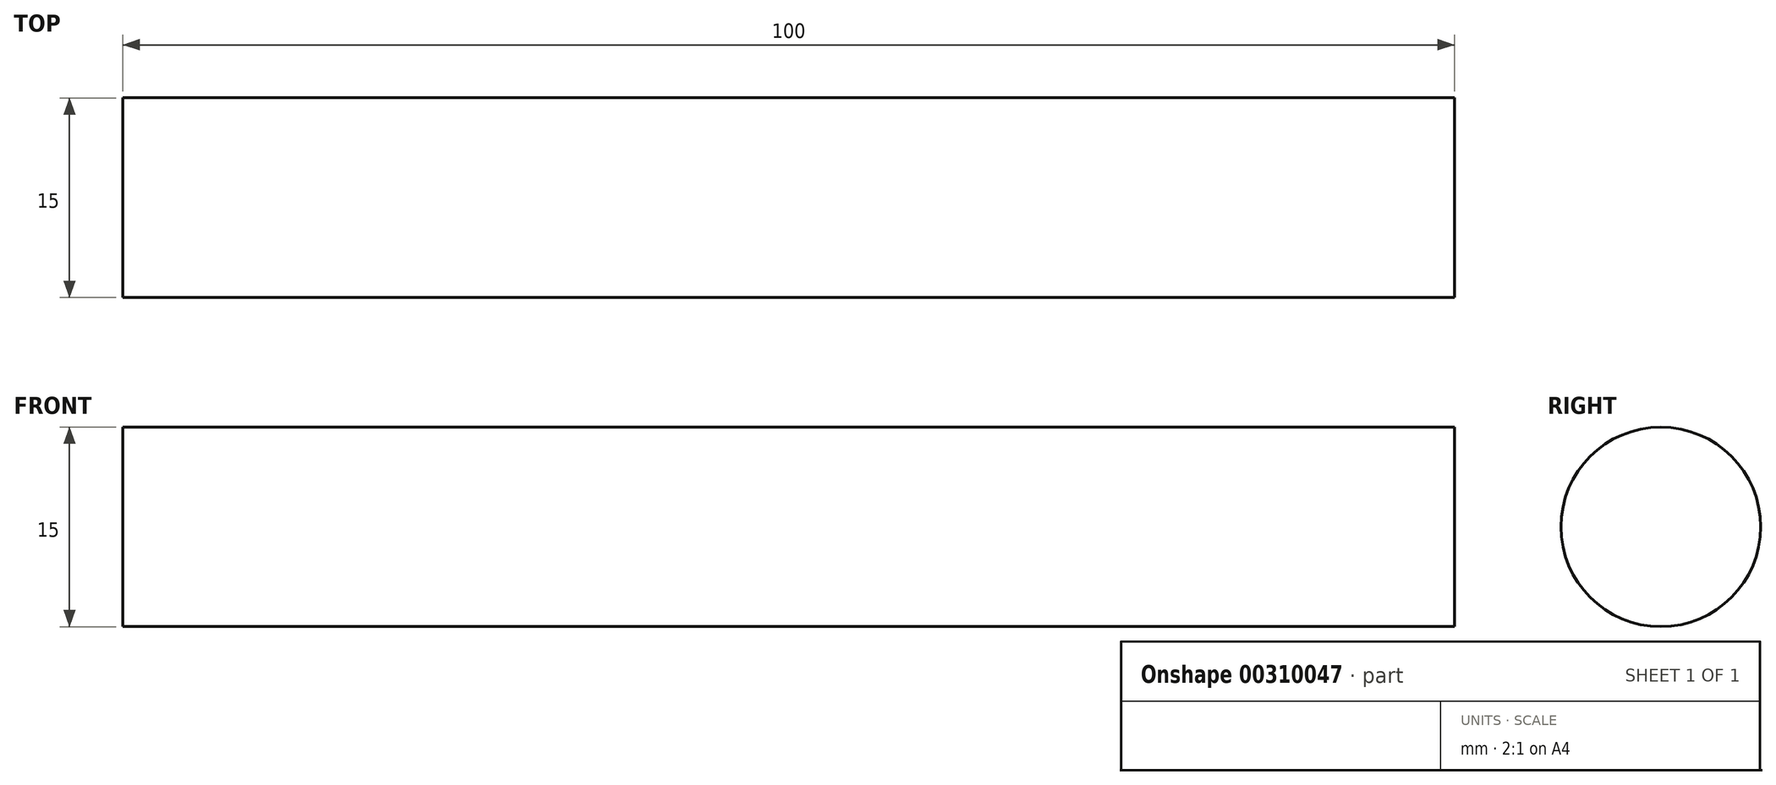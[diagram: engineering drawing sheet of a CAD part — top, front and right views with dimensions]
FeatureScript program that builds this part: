
annotation { "Feature Type Name" : "Feature", "Feature Type Description" : "" }
export const myFeature = defineFeature(function(context is Context, id is Id, definition is map)
    precondition{}
    {
        {
            var Q0;
            Q0=qCreatedBy(makeId("Top.planeOp"),FACE);
            var sketch = newSketch(context, id + "F0", { "sketchPlane" : qUnion([Q0])});
            skLineSegment(sketch, "E0.bottom", {"start": v(0, 0) * mm, "end": v(94.23, 0) * mm});
            skLineSegment(sketch, "E0.top", {"start": v(0, 10.6) * mm, "end": v(94.23, 10.6) * mm});
            skLineSegment(sketch, "E0.left", {"start": v(0, 0) * mm, "end": v(0, 10.6) * mm});
            skLineSegment(sketch, "E0.right", {"start": v(94.23, 0) * mm, "end": v(94.23, 10.6) * mm});
            skSolve(sketch);
        }
        {
            var Q0;
            Q0=makeQuery(id+"F0.imprint","IMPRINT",FACE,{"disambiguationData":[TD([[makeQuery(id+"F0.imprint","IMPRINT",EDGE,{"derivedFrom":sQuery(id+"F0.wireOp",EDGE,"E0.bottom")}),1.0]])]});
            extrude(context, id + "F1", {"entities" : qUnion([Q0]), "depth" : 10.6 * mm});
        }
        {
            var Q0;
            Q0=makeQuery(id+"F1.opExtrude","SWEPT_FACE",FACE,{"disambiguationData":[OSD([sQuery(id+"F0.wireOp",EDGE,"E0.right")])]});
            var sketch = newSketch(context, id + "F2", { "sketchPlane" : qUnion([Q0])});
            skLineSegment(sketch, "E1", {"start": v(0, 0) * mm, "end": v(10.6, 10.6) * mm});
            skCircle(sketch, "E2", {"center": v(5.3, 5.3) * mm, "radius": 7.5 * mm});
            skSolve(sketch);
        }
        {
            var Q0;
            Q0 = qSketchRegion(id + "F2", true);
            extrude(context, id + "F3", {"entities" : qUnion([Q0]), "operationType" : NewBodyOperationType.ADD, "oppositeDirection" : true, "depth" : 100 * mm});
        }
    });
